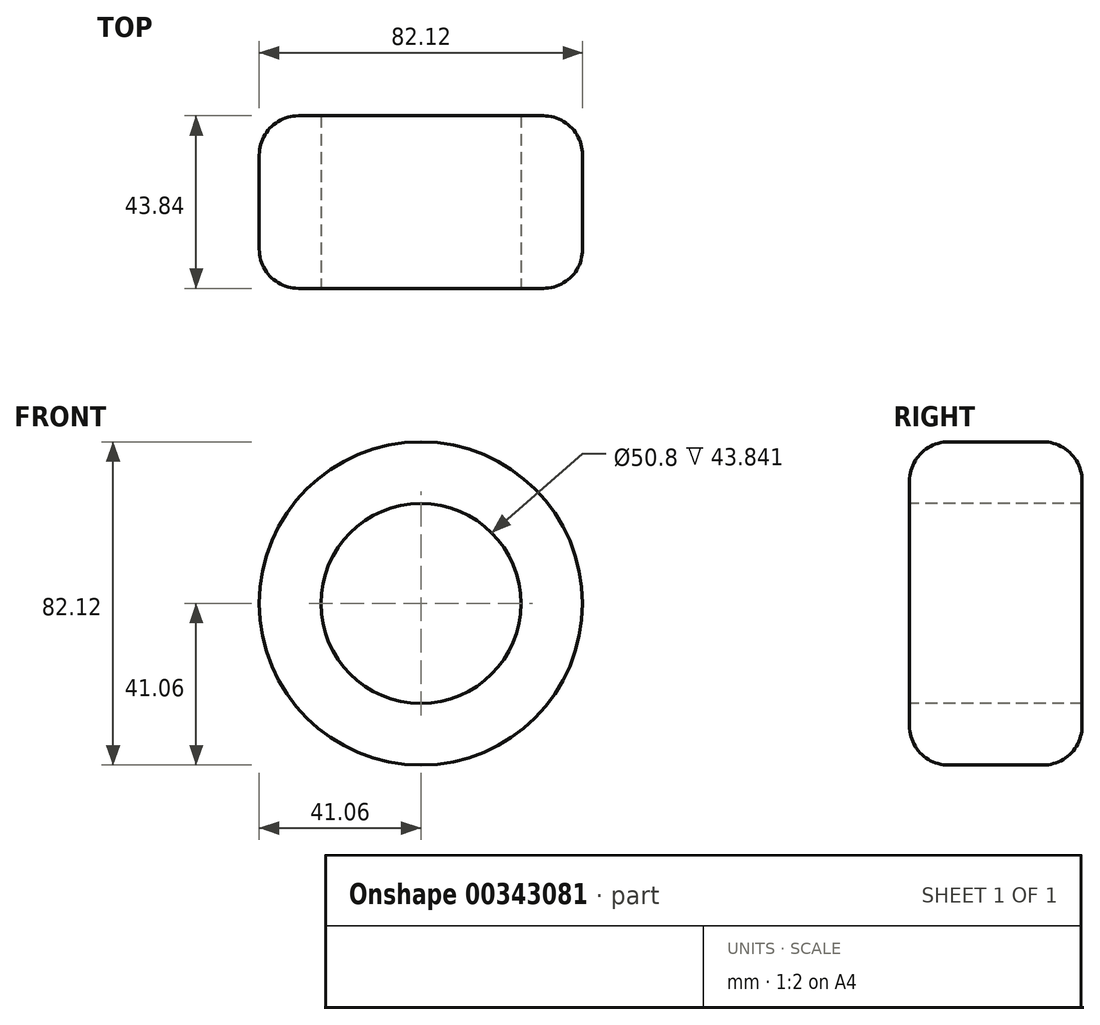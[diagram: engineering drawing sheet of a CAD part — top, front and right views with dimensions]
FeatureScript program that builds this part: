
annotation { "Feature Type Name" : "Feature", "Feature Type Description" : "" }
export const myFeature = defineFeature(function(context is Context, id is Id, definition is map)
    precondition{}
    {
        {
            var Q0;
            Q0=qCreatedBy(makeId("Front.planeOp"),FACE);
            var sketch = newSketch(context, id + "F0", { "sketchPlane" : qUnion([Q0])});
            skCircle(sketch, "E0", {"center": v(0, 0) * mm, "radius": 41.06 * mm});
            skSolve(sketch);
        }
        {
            var Q0;
            Q0 = qSketchRegion(id + "F0", true);
            extrude(context, id + "F1", {"entities" : qUnion([Q0]), "depth" : 43.84 * mm});
        }
        {
            var Q0;
            Q0=makeQuery(id+"F1.opExtrude","CAP_EDGE",EDGE,{"disambiguationData":[OSD([sQuery(id+"F0.wireOp",EDGE,"E0")])],"isStart":false});
            var Q1;
            Q1=makeQuery(id+"F1.opExtrude","SWEPT_FACE",FACE,{"disambiguationData":[OSD([sQuery(id+"F0.wireOp",EDGE,"E0")])]});
            fillet(context, id + "F2", {"entities" : qUnion([Q0, Q1]), "radius" : 9.94 * mm, "tangentPropagation" : true, "allowEdgeOverflow" : false});
        }
        {
            var Q0;
            Q0=makeQuery(id+"F1.opExtrude","CAP_FACE",FACE,{"disambiguationData":[OSD([sQuery(id+"F0.wireOp",EDGE,"E0")])],"isStart":false});
            var sketch = newSketch(context, id + "F3", { "sketchPlane" : qUnion([Q0])});
            skCircle(sketch, "E1", {"center": v(0, 0) * mm, "radius": 23.13 * mm});
            skSolve(sketch);
        }
        {
            var Q0;
            Q0=makeQuery(id+"F3.imprint","IMPRINT",FACE,{"disambiguationData":[TD([[makeQuery(id+"F3.imprint","IMPRINT",EDGE,{"derivedFrom":sQuery(id+"F3.wireOp",EDGE,"E1")}),1.0]])]});
            var sketch = newSketch(context, id + "F4", { "sketchPlane" : qUnion([Q0])});
            skSolve(sketch);
        }
        {
            var Q0;
            Q0=makeQuery(id+"F4.imprint","IMPRINT",FACE,{"disambiguationData":[TD([[makeQuery(id+"F4.imprint","IMPRINT",EDGE,{"derivedFrom":makeQuery(id+"F3.imprint","IMPRINT",EDGE,{"derivedFrom":sQuery(id+"F3.wireOp",EDGE,"E1")})}),1.0]])]});
            extrude(context, id + "F5", {"entities" : qUnion([Q0]), "operationType" : NewBodyOperationType.ADD, "oppositeDirection" : true, "depth" : 27.27 * mm});
        }
        {
            var Q0;
            Q0=sQuery(id+"F3.wireOp",VERTEX,"E1.center");
            var Q1;
            Q1=makeQuery(id+"F1.opExtrude","SWEPT_BODY",BODY,{"disambiguationData":[OSD([sQuery(id+"F0.wireOp",EDGE,"E0")])]});
            hole(context, id + "F6", {"style" : HoleStyle.SIMPLE, "endStyle" : HoleEndStyle.THROUGH, "holeDiameter" : 50.8 * mm, "isTappedThrough" : true, "tappedDepth" : 12.7 * mm, "tapClearance" : 3, "locations" : qUnion([Q0]), "scope" : qUnion([Q1])});
        }
    });
